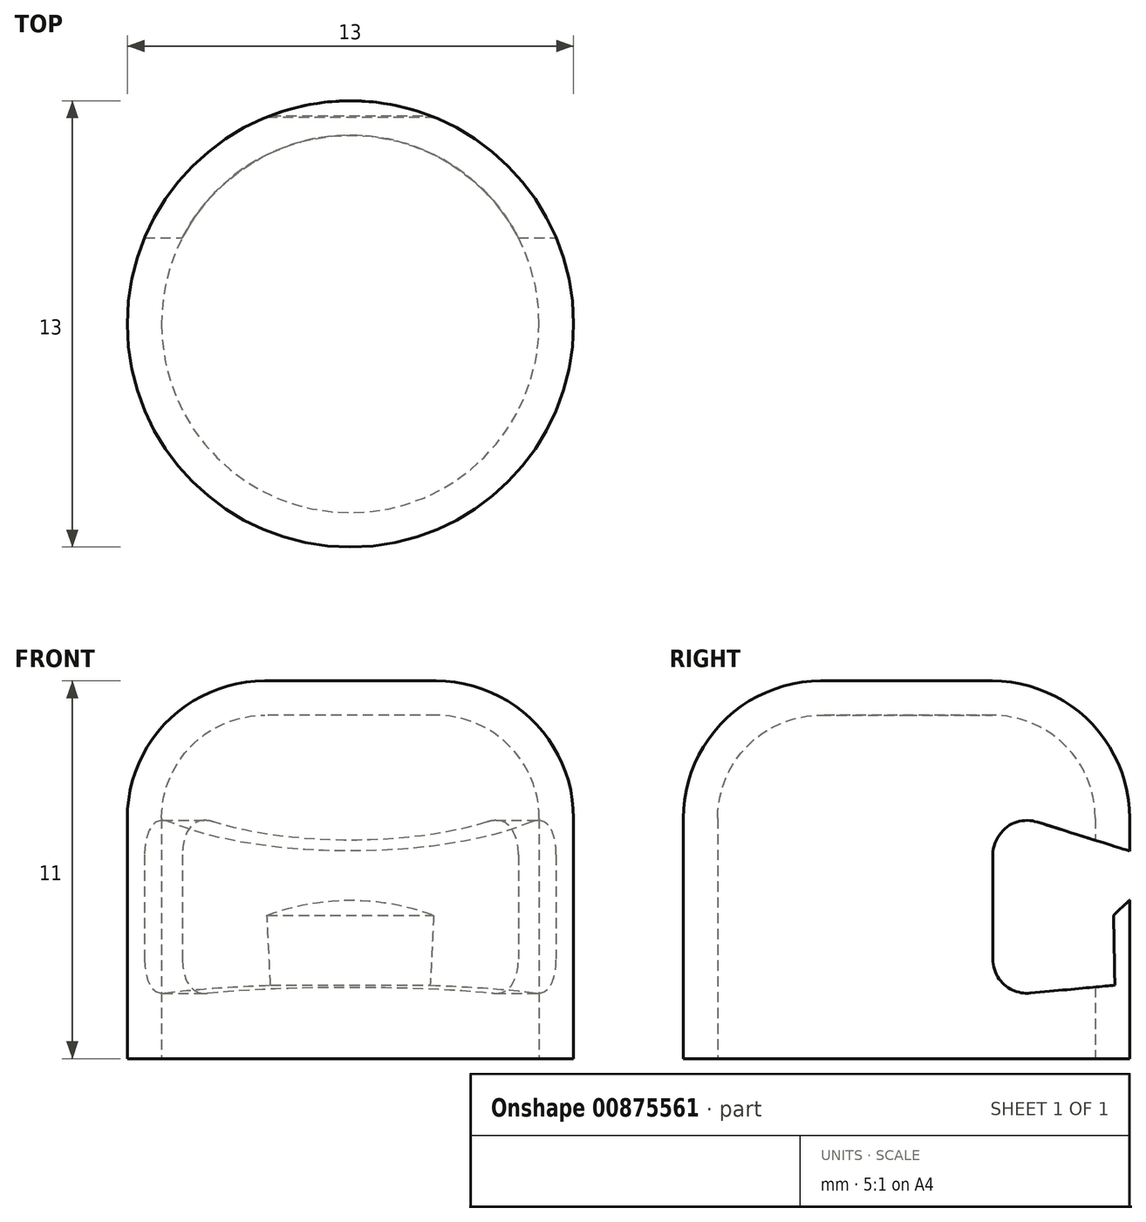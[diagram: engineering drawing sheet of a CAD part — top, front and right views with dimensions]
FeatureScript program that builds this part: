
annotation { "Feature Type Name" : "Feature", "Feature Type Description" : "" }
export const myFeature = defineFeature(function(context is Context, id is Id, definition is map)
    precondition{}
    {
        {
            var Q0;
            Q0=qCreatedBy(makeId("Top.planeOp"),FACE);
            var sketch = newSketch(context, id + "F0", { "sketchPlane" : qUnion([Q0])});
            skCircle(sketch, "E0", {"center": v(0, 0) * mm, "radius": 6.5 * mm});
            skSolve(sketch);
        }
        {
            var Q0;
            Q0 = qSketchRegion(id + "F0", true);
            extrude(context, id + "F1", {"entities" : qUnion([Q0]), "depth" : 11 * mm, "offsetDistance" : 25 * mm});
        }
        {
            var Q0;
            Q0=makeQuery(id+"F1.opExtrude","CAP_EDGE",EDGE,{"disambiguationData":[OSD([sQuery(id+"F0.wireOp",EDGE,"E0")])],"isStart":false});
            fillet(context, id + "F2", {"entities" : qUnion([Q0]), "radius" : 4 * mm, "tangentPropagation" : true, "allowEdgeOverflow" : false});
        }
        {
            var Q0;
            Q0=makeQuery(id+"F1.opExtrude","CAP_FACE",FACE,{"disambiguationData":[OSD([sQuery(id+"F0.wireOp",EDGE,"E0")])],"isStart":true});
            shell(context, id + "F3", {"entities" : qUnion([Q0]), "thickness" : 1 * mm});
        }
        {
            var Q0;
            Q0=qCreatedBy(makeId("Right.planeOp"),FACE);
            var sketch = newSketch(context, id + "F4", { "sketchPlane" : qUnion([Q0])});
            skLineSegment(sketch, "E1", {"start": v(7.64, 5.69) * mm, "end": v(3.81, 6.89) * mm});
            skLineSegment(sketch, "E2", {"start": v(2.51, 5.94) * mm, "end": v(2.51, 2.9) * mm});
            skLineSegment(sketch, "E3", {"start": v(3.6, 1.9) * mm, "end": v(6.07, 2.14) * mm});
            skPoint(sketch, "E4.visualSharp", {"position": v(2.51, 7.3) * mm});
            skArc(sketch, "E4.filletArc", {"start": v(3.81, 6.89) * mm, "mid": v(2.92, 6.74) * mm, "end": v(2.51, 5.94) * mm});
            skPoint(sketch, "E5.visualSharp", {"position": v(2.51, 1.8) * mm});
            skArc(sketch, "E5.filletArc", {"start": v(2.51, 2.9) * mm, "mid": v(2.84, 2.16) * mm, "end": v(3.6, 1.9) * mm});
            skLineSegment(sketch, "E6", {"start": v(6.07, 2.14) * mm, "end": v(6.03, 4.18) * mm});
            skLineSegment(sketch, "E7", {"start": v(6.03, 4.18) * mm, "end": v(7.64, 5.69) * mm});
            skSolve(sketch);
        }
        {
            var Q0;
            Q0=makeQuery(id+"F4.imprint","IMPRINT",FACE,{"disambiguationData":[TD([[makeQuery(id+"F4.imprint","IMPRINT",EDGE,{"derivedFrom":sQuery(id+"F4.wireOp",EDGE,"E1")}),1.0]])]});
            extrude(context, id + "F5", {"entities" : qUnion([Q0]), "operationType" : NewBodyOperationType.REMOVE, "endBound" : BoundingType.SYMMETRIC, "oppositeDirection" : true, "depth" : 25 * mm, "offsetDistance" : 25 * mm});
        }
    });
